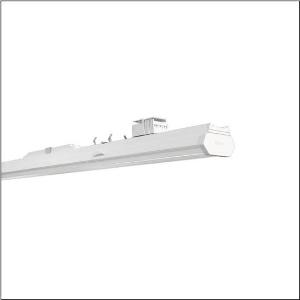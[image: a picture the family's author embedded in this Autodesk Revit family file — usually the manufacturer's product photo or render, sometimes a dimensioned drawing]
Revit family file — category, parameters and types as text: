
# Revit family: licross_r__11_protected_mo_51tp12dn495g3c_6ec9
name_source: partatom
category: Lighting Fixtures
units: mm (PartAtom-declared; Revit-internal decimal feet)

## family parameters
Cut with Voids When Loaded = No
Host = Face
Light Source = No
Part Type = Normal
Room Calculation Point = No
Round Connector Dimension = Use Diameter
Shared = No

## types (1)
- --- (1 x LED, 980 lm, 6.8 W, 4000K)
    Apparent Load = 7 VA
    CIE Flux Codes = 73 92 98 99 100
    Color Rendering = 80
    Color Temperature = 4000K
    Default Elevation = 1800 mm
    Description = Licross® 11 Protected MO, luminaire insert, of sheet steel, galvanised, coil coated, white, length: 1.500mm, width: 90mm, height: 101mm, LED rated luminous flux: 9.980lm, light colour: 840, control gear: DALI 2, with plug, 6-pole, with phase selection, for trunking rail, 14-core, mains connection: 220..240V, AC, 50/60Hz, rated input power: 61W, for trunking rail, 14-core, halogen-free wiring, for emergency light function, converter,control gear: single battery element, battery: LiFeP04, 9Ah, primary light control with lens, of plastic, primary optical cover: cover, of PMMA, light emission: direct distribution, primary light characteristic: symmetric, protection rating (complete): IP64, insulation class (complete): insulation class I (protective earthing), certification: CE, UKCA, protection symbol: D if used in an environment with conductive dust loads with corresponding accessories, impact resistance: IK06, permissible ambient temperature for indoor applications: +5..+35°C, standard: EN 60598-2-22, LABS conformity tested according to VDMA 24364:2018-05, reducing of maximum allowable ambient temperature of 5°C with ceiling mounting, corresponds to IFS (International Featured Standards) requirements for safety and quality in the food industry, packaging unit: 1 piece
    Height = 92 mm
    Lamp = 1 x LED
    Lamp Light Flux = 980 lm
    Lamp Power = 6.8 W
    Lamp count = 1
    Length = 1500 mm
    Luminous efficacy = 144 lm/W
    Manufacturer = Siteco
    ModVariant = No
    Model = 51TP12DN495G3C
    Mounting Place = Ceiling
    Mounting Type = Pendant
    Number of Poles = 1
    OnlyDefault = Yes
    Power Factor = 1
    Product Name = Licross® 11 Protected MO
    Product group = luminaire insert
    ProductGroupID = 901
    Protection Class = Protection class I
    Protection Degree = IP 64
    RLX_Detail_Level = 1
    RLX_Emergency_Light_Flux = 0 lm
    RLX_Emergency_Type = 0
    RLX_Emergency_Type_DB = No
    RlxData = <blob elided: 24757 chars, md5=c473d1b0>
    Socket = socket
    Standby Power = 0 W
    System Light Flux = 980 lm
    System Power = 7 W
    Type Comments = : emergency light operation: 3 h
    Type Image = l_1256148.jpg
    URL = http://relux.com
    VarID = @adj_041215
    Voltage = 0 V
    Weight = 0.00 kg
    Width = 88 mm

## geometry (parser evidence)
native form markers: Blend x4, Sweep x9
no freeform markers — native parametric forms only
